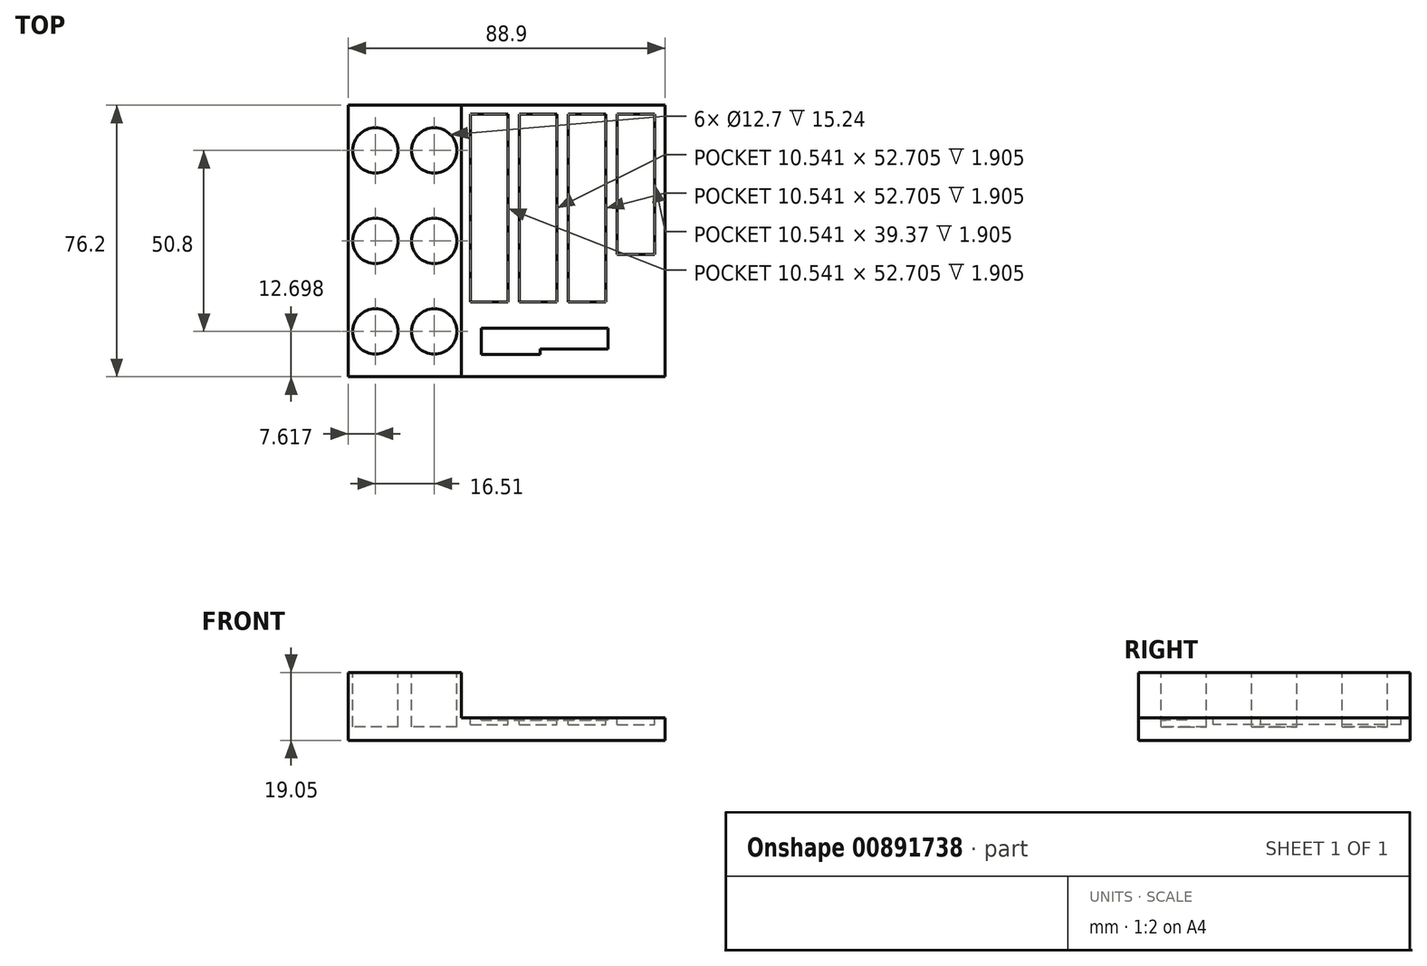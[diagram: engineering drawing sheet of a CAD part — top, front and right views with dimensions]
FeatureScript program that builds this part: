
annotation { "Feature Type Name" : "Feature", "Feature Type Description" : "" }
export const myFeature = defineFeature(function(context is Context, id is Id, definition is map)
    precondition{}
    {
        {
            var Q0;
            Q0=qCreatedBy(makeId("Top.planeOp"),FACE);
            var sketch = newSketch(context, id + "F0", { "sketchPlane" : qUnion([Q0])});
            skLineSegment(sketch, "E0.bottom", {"start": v(-40.86, -49.22) * mm, "end": v(48.04, -49.22) * mm});
            skLineSegment(sketch, "E0.top", {"start": v(-40.86, 26.98) * mm, "end": v(48.04, 26.98) * mm});
            skLineSegment(sketch, "E0.left", {"start": v(-40.86, -49.22) * mm, "end": v(-40.86, 26.98) * mm});
            skLineSegment(sketch, "E0.right", {"start": v(48.04, -49.22) * mm, "end": v(48.04, 26.98) * mm});
            skLineSegment(sketch, "E1.bottom", {"start": v(-40.86, 26.98) * mm, "end": v(-9.11, 26.98) * mm});
            skLineSegment(sketch, "E1.top", {"start": v(-40.86, -49.22) * mm, "end": v(-9.11, -49.22) * mm});
            skLineSegment(sketch, "E1.left", {"start": v(-40.86, 26.98) * mm, "end": v(-40.86, -49.22) * mm});
            skLineSegment(sketch, "E1.right", {"start": v(-9.11, 26.98) * mm, "end": v(-9.11, -49.22) * mm});
            skSolve(sketch);
        }
        {
            var Q0;
            {var subQ2=sQuery(id+"F0.wireOp",EDGE,"E0.left");Q0=makeQuery(id+"F0.imprint","IMPRINT",FACE,{"disambiguationData":[TD([[makeQuery(id+"F0.imprint","IMPRINT",EDGE,{"derivedFrom":subQ2}),-1.0]])]});}
            extrude(context, id + "F1", {"entities" : qUnion([Q0]), "depth" : 19.05 * mm, "offsetDistance" : 25.4 * mm});
        }
        {
            var Q0;
            {var subQ3=sQuery(id+"F0.wireOp",EDGE,"E0.left");var subQ7=sQuery(id+"F0.wireOp",EDGE,"E0.right");Q0=qUnion([makeQuery(id+"F0.imprint","IMPRINT",FACE,{"disambiguationData":[TD([[makeQuery(id+"F0.imprint","IMPRINT",EDGE,{"derivedFrom":subQ7}),1.0]])]}),makeQuery(id+"F0.imprint","IMPRINT",FACE,{"disambiguationData":[TD([[makeQuery(id+"F0.imprint","IMPRINT",EDGE,{"derivedFrom":subQ3}),-1.0]])]})]);}
            extrude(context, id + "F2", {"entities" : qUnion([Q0]), "operationType" : NewBodyOperationType.ADD, "depth" : 6.35 * mm, "offsetDistance" : 25.4 * mm});
        }
        {
            var Q0;
            Q0=makeQuery(id+"F1.opExtrude","CAP_FACE",FACE,{"disambiguationData":[OSD([sQuery(id+"F0.wireOp",EDGE,"E0.bottom"),sQuery(id+"F0.wireOp",EDGE,"E0.top"),sQuery(id+"F0.wireOp",EDGE,"E0.left"),sQuery(id+"F0.wireOp",EDGE,"E1.right")])],"isStart":false});
            var sketch = newSketch(context, id + "F3", { "sketchPlane" : qUnion([Q0])});
            skCircle(sketch, "E2", {"center": v(-33.24, 14.28) * mm, "radius": 6.35 * mm});
            skCircle(sketch, "E3", {"center": v(-16.73, 14.28) * mm, "radius": 6.35 * mm});
            skCircle(sketch, "E4", {"center": v(-33.24, -11.12) * mm, "radius": 6.35 * mm});
            skCircle(sketch, "E5", {"center": v(-16.73, -11.12) * mm, "radius": 6.35 * mm});
            skCircle(sketch, "E6", {"center": v(-33.24, -36.52) * mm, "radius": 6.35 * mm});
            skCircle(sketch, "E7", {"center": v(-16.73, -36.52) * mm, "radius": 6.35 * mm});
            skSolve(sketch);
        }
        {
            var Q0;
            Q0=makeQuery(id+"F3.imprint","IMPRINT",FACE,{"disambiguationData":[TD([[makeQuery(id+"F3.imprint","IMPRINT",EDGE,{"derivedFrom":sQuery(id+"F3.wireOp",EDGE,"E2")}),1.0]])]});
            var Q1;
            Q1=makeQuery(id+"F3.imprint","IMPRINT",FACE,{"disambiguationData":[TD([[makeQuery(id+"F3.imprint","IMPRINT",EDGE,{"derivedFrom":sQuery(id+"F3.wireOp",EDGE,"E3")}),1.0]])]});
            var Q2;
            Q2=makeQuery(id+"F3.imprint","IMPRINT",FACE,{"disambiguationData":[TD([[makeQuery(id+"F3.imprint","IMPRINT",EDGE,{"derivedFrom":sQuery(id+"F3.wireOp",EDGE,"E4")}),1.0]])]});
            var Q3;
            Q3=makeQuery(id+"F3.imprint","IMPRINT",FACE,{"disambiguationData":[TD([[makeQuery(id+"F3.imprint","IMPRINT",EDGE,{"derivedFrom":sQuery(id+"F3.wireOp",EDGE,"E5")}),1.0]])]});
            var Q4;
            Q4=makeQuery(id+"F3.imprint","IMPRINT",FACE,{"disambiguationData":[TD([[makeQuery(id+"F3.imprint","IMPRINT",EDGE,{"derivedFrom":sQuery(id+"F3.wireOp",EDGE,"E7")}),1.0]])]});
            var Q5;
            Q5=makeQuery(id+"F3.imprint","IMPRINT",FACE,{"disambiguationData":[TD([[makeQuery(id+"F3.imprint","IMPRINT",EDGE,{"derivedFrom":sQuery(id+"F3.wireOp",EDGE,"E6")}),1.0]])]});
            extrude(context, id + "F4", {"entities" : qUnion([Q0, Q1, Q2, Q3, Q4, Q5]), "operationType" : NewBodyOperationType.REMOVE, "oppositeDirection" : true, "depth" : 15.24 * mm, "offsetDistance" : 25.4 * mm});
        }
        {
            var Q0;
            Q0=makeQuery(id+"F2.opExtrude","CAP_FACE",FACE,{"disambiguationData":[OSD([sQuery(id+"F0.wireOp",EDGE,"E0.bottom"),sQuery(id+"F0.wireOp",EDGE,"E0.top"),sQuery(id+"F0.wireOp",EDGE,"E0.left"),sQuery(id+"F0.wireOp",EDGE,"E0.right")])],"isStart":false});
            var sketch = newSketch(context, id + "F5", { "sketchPlane" : qUnion([Q0])});
            skLineSegment(sketch, "E8.bottom", {"start": v(34.57, 24.44) * mm, "end": v(45.12, 24.44) * mm});
            skLineSegment(sketch, "E8.top", {"start": v(34.57, -14.93) * mm, "end": v(45.12, -14.93) * mm});
            skLineSegment(sketch, "E8.left", {"start": v(34.57, 24.44) * mm, "end": v(34.57, -14.93) * mm});
            skLineSegment(sketch, "E8.right", {"start": v(45.12, 24.44) * mm, "end": v(45.12, -14.93) * mm});
            skLineSegment(sketch, "E9.bottom", {"start": v(-6.57, 24.44) * mm, "end": v(3.97, 24.44) * mm});
            skLineSegment(sketch, "E9.top", {"start": v(-6.57, -28.27) * mm, "end": v(3.97, -28.27) * mm});
            skLineSegment(sketch, "E9.left", {"start": v(-6.57, 24.44) * mm, "end": v(-6.57, -28.27) * mm});
            skLineSegment(sketch, "E9.right", {"start": v(3.97, 24.44) * mm, "end": v(3.97, -28.27) * mm});
            skLineSegment(sketch, "E10.bottom", {"start": v(7.14, 24.44) * mm, "end": v(17.68, 24.44) * mm});
            skLineSegment(sketch, "E10.top", {"start": v(7.14, -28.27) * mm, "end": v(17.68, -28.27) * mm});
            skLineSegment(sketch, "E10.left", {"start": v(7.14, 24.44) * mm, "end": v(7.14, -28.27) * mm});
            skLineSegment(sketch, "E10.right", {"start": v(17.68, 24.44) * mm, "end": v(17.68, -28.27) * mm});
            skLineSegment(sketch, "E11.bottom", {"start": v(20.86, 24.44) * mm, "end": v(31.4, 24.44) * mm});
            skLineSegment(sketch, "E11.top", {"start": v(20.86, -28.27) * mm, "end": v(31.4, -28.27) * mm});
            skLineSegment(sketch, "E11.left", {"start": v(20.86, 24.44) * mm, "end": v(20.86, -28.27) * mm});
            skLineSegment(sketch, "E11.right", {"start": v(31.4, 24.44) * mm, "end": v(31.4, -28.27) * mm});
            skLineSegment(sketch, "E12.bottom", {"start": v(-3.56, -35.65) * mm, "end": v(32, -35.65) * mm});
            skLineSegment(sketch, "E12.top", {"start": v(-3.56, -43.02) * mm, "end": v(32, -43.02) * mm});
            skLineSegment(sketch, "E12.left", {"start": v(-3.56, -35.65) * mm, "end": v(-3.56, -43.02) * mm});
            skLineSegment(sketch, "E12.right", {"start": v(32, -35.65) * mm, "end": v(32, -43.02) * mm});
            skLineSegment(sketch, "E13.bottom", {"start": v(32, -43.02) * mm, "end": v(12.95, -43.02) * mm});
            skLineSegment(sketch, "E13.top", {"start": v(32, -41.5) * mm, "end": v(12.95, -41.5) * mm});
            skLineSegment(sketch, "E13.left", {"start": v(32, -43.02) * mm, "end": v(32, -41.5) * mm});
            skLineSegment(sketch, "E13.right", {"start": v(12.95, -43.02) * mm, "end": v(12.95, -41.5) * mm});
            skSolve(sketch);
        }
        {
            var Q0;
            Q0=makeQuery(id+"F5.imprint","IMPRINT",FACE,{"disambiguationData":[TD([[makeQuery(id+"F5.imprint","IMPRINT",EDGE,{"derivedFrom":sQuery(id+"F5.wireOp",EDGE,"E10.bottom")}),-1.0]])]});
            var Q1;
            Q1=makeQuery(id+"F5.imprint","IMPRINT",FACE,{"disambiguationData":[TD([[makeQuery(id+"F5.imprint","IMPRINT",EDGE,{"derivedFrom":sQuery(id+"F5.wireOp",EDGE,"E9.bottom")}),-1.0]])]});
            var Q2;
            Q2=makeQuery(id+"F5.imprint","IMPRINT",FACE,{"disambiguationData":[TD([[makeQuery(id+"F5.imprint","IMPRINT",EDGE,{"derivedFrom":sQuery(id+"F5.wireOp",EDGE,"E8.bottom")}),-1.0]])]});
            var Q3;
            Q3=makeQuery(id+"F5.imprint","IMPRINT",FACE,{"disambiguationData":[TD([[makeQuery(id+"F5.imprint","IMPRINT",EDGE,{"derivedFrom":sQuery(id+"F5.wireOp",EDGE,"E11.bottom")}),-1.0]])]});
            var Q4;
            Q4=makeQuery(id+"F5.imprint","IMPRINT",FACE,{"disambiguationData":[TD([[makeQuery(id+"F5.imprint","IMPRINT",EDGE,{"derivedFrom":sQuery(id+"F5.wireOp",EDGE,"E12.bottom")}),-1.0]])]});
            extrude(context, id + "F6", {"entities" : qUnion([Q0, Q1, Q2, Q3, Q4]), "operationType" : NewBodyOperationType.REMOVE, "oppositeDirection" : true, "depth" : 1.9 * mm, "offsetDistance" : 25.4 * mm});
        }
        {
            var Q0;
            Q0=makeQuery(id+"F6.boolean.opBoolean","COPY",FACE,{"derivedFrom":makeQuery(id+"F6.opExtrude","CAP_FACE",FACE,{"disambiguationData":[OSD([sQuery(id+"F5.wireOp",EDGE,"E12.bottom"),sQuery(id+"F5.wireOp",EDGE,"E12.top"),sQuery(id+"F5.wireOp",EDGE,"E12.left"),sQuery(id+"F5.wireOp",EDGE,"E12.right"),sQuery(id+"F5.wireOp",EDGE,"E13.top"),sQuery(id+"F5.wireOp",EDGE,"E13.right")])],"isStart":false})});
            extrude(context, id + "F7", {"entities" : qUnion([Q0]), "operationType" : NewBodyOperationType.ADD, "depth" : 1.27 * mm, "offsetDistance" : 25.4 * mm});
        }
    });
